# Revit family: Б409_RV17_LOD400 (05.11.23)
name_source: partatom
category: Электрооборудование
revit_build: Autodesk Revit 2017 (Build: 20170118_1100(x64)
units: mm (PartAtom-declared; Revit-internal decimal feet)

## family parameters
Всегда вертикально = Нет
Конфигурация панели = Два столбца, слева направо
На основе рабочей плоскости = Да
Общий = Нет
При загрузке вырезать с полостями = Нет
Размер круглого соединителя = Использовать диаметр
Тип детали = Щит
Точка расчета площади = Нет

## types (1)
- Б409
    ADSK_URL страницы изделия = https://stilsoft.ru
    ADSK_Единица измерения = шт.
    ADSK_Завод-изготовитель = ООО «Основа Безопасности»
    ADSK_Количество = 1
    ADSK_Марка = СТВФ.426484.041ПС
    ADSK_Масса = 0.7
    ADSK_Наименование = Контроллер Б409
    ADSK_Размер_Высота = 42 мм
    ADSK_Размер_Глубина = 110 мм
    ADSK_Размер_Длина = 200 мм
    d_короба = 20 мм
    Длина кода ключа (пропуска), символов = 1-8
    Интерфейс считывателей = Wiegand 26, Wiegand 40/42
    Информационная ёмкость (количество ШС) = 8
    Количество поддерживаемых считывающих устройств, не более, шт. = 2
    Максимальное количество извещателей ОС на 1 шлейф сигнализации, не более, шт. = 20
    Максимальное количество ключей (пропусков) ОС, шт. = 16
    Максимальное удаление считывателей от контроллера, не более, м = 100 мм
    Максимальный потребляемый ток, (без дополнительных внешних потребителей по сети постоянного тока) не более, А = 0 А
    Напряжение = 12
    Отметка по умолчанию = 1219 мм
    Предельное значение сопротивления проводов ШС, кОм = 0.1
    Стандарт интерфейса связи = 10 Base-T Ethernet (гнездо RJ-45)
